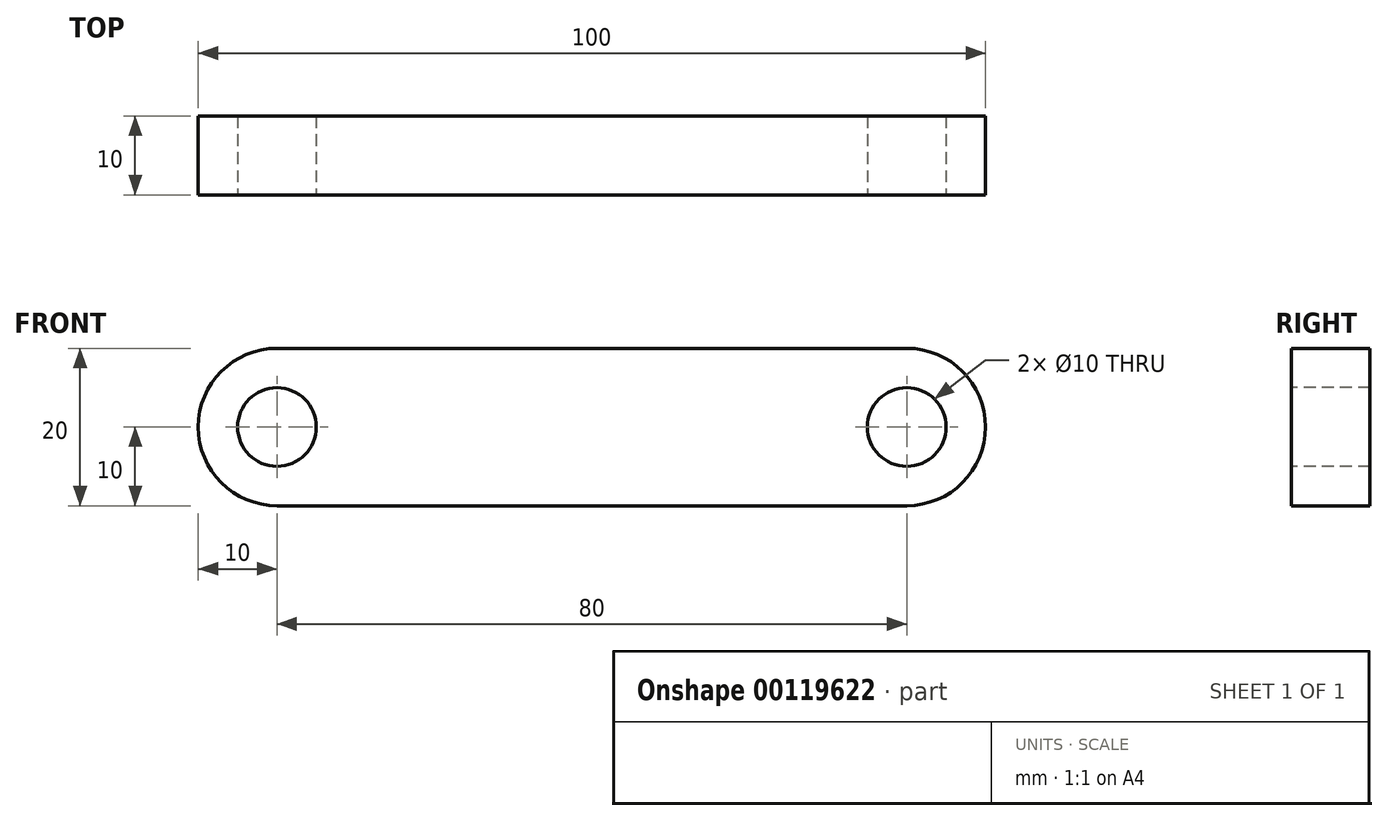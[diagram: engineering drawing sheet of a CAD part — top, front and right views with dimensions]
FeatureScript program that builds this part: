
annotation { "Feature Type Name" : "Feature", "Feature Type Description" : "" }
export const myFeature = defineFeature(function(context is Context, id is Id, definition is map)
    precondition{}
    {
        {
            var Q0;
            Q0=qCreatedBy(makeId("Front.planeOp"),FACE);
            var sketch = newSketch(context, id + "F0", { "sketchPlane" : qUnion([Q0])});
            skLineSegment(sketch, "E0.bottom", {"start": v(0, 0) * mm, "end": v(80, 0) * mm});
            skLineSegment(sketch, "E0.top", {"start": v(0, 20) * mm, "end": v(80, 20) * mm});
            skArc(sketch, "E1", {"start": v(0, 20) * mm, "mid": v(-10, 10) * mm, "end": v(0, 0) * mm});
            skArc(sketch, "E2", {"start": v(80, 0) * mm, "mid": v(90, 10) * mm, "end": v(80, 20) * mm});
            skSolve(sketch);
        }
        {
            var Q0;
            Q0 = qSketchRegion(id + "F0", true);
            extrude(context, id + "F1", {"entities" : qUnion([Q0]), "depth" : 10 * mm});
        }
        {
            var Q0;
            Q0=makeQuery(id+"F1.opExtrude","CAP_FACE",FACE,{"disambiguationData":[OSD([sQuery(id+"F0.wireOp",EDGE,"E0.bottom"),sQuery(id+"F0.wireOp",EDGE,"E0.top"),sQuery(id+"F0.wireOp",EDGE,"E1"),sQuery(id+"F0.wireOp",EDGE,"E2")])],"isStart":false});
            var sketch = newSketch(context, id + "F2", { "sketchPlane" : qUnion([Q0])});
            skCircle(sketch, "E3", {"center": v(0, 10) * mm, "radius": 5 * mm});
            skCircle(sketch, "E4", {"center": v(80, 10) * mm, "radius": 5 * mm});
            skSolve(sketch);
        }
        {
            var Q0;
            Q0 = qSketchRegion(id + "F2", true);
            extrude(context, id + "F3", {"entities" : qUnion([Q0]), "operationType" : NewBodyOperationType.REMOVE, "endBound" : BoundingType.THROUGH_ALL, "oppositeDirection" : true, "depth" : 25 * mm});
        }
    });
